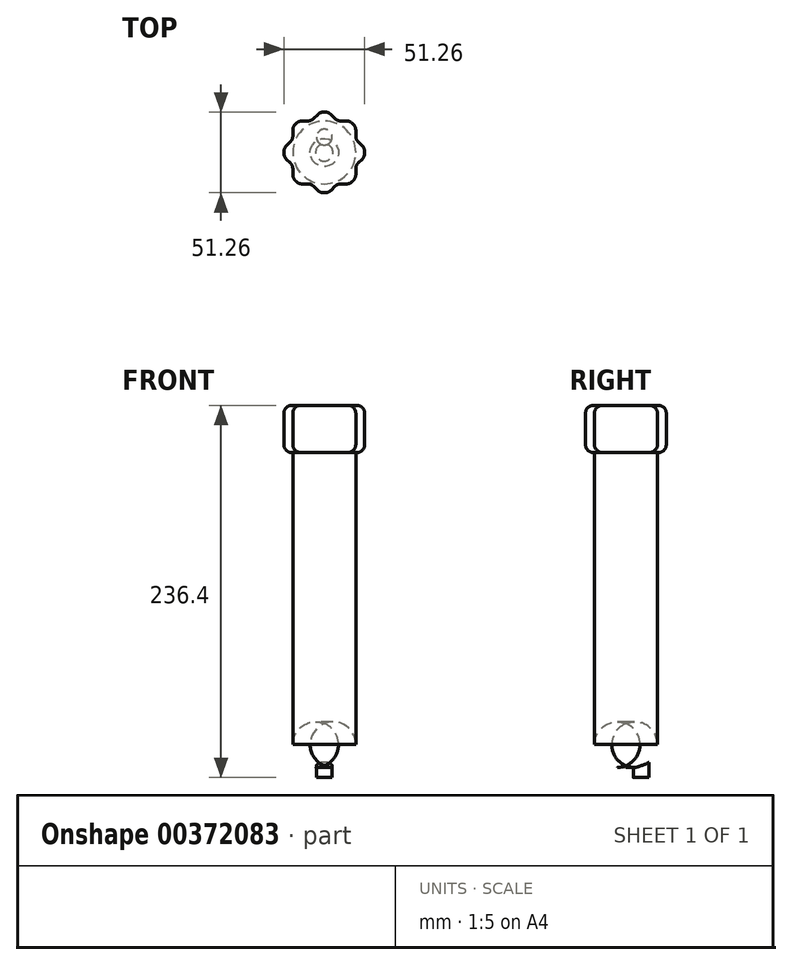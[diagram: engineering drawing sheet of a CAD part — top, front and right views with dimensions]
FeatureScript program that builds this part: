
annotation { "Feature Type Name" : "Feature", "Feature Type Description" : "" }
export const myFeature = defineFeature(function(context is Context, id is Id, definition is map)
    precondition{}
    {
        {
            var Q0;
            Q0=qCreatedBy(makeId("Top.planeOp"),FACE);
            var sketch = newSketch(context, id + "F0", { "sketchPlane" : qUnion([Q0])});
            skCircle(sketch, "E0", {"center": v(0, 0) * mm, "radius": 20 * mm});
            skSolve(sketch);
        }
        {
            var Q0;
            Q0 = qSketchRegion(id + "F0", true);
            extrude(context, id + "F1", {"entities" : qUnion([Q0]), "depth" : 200 * mm});
        }
        {
            var Q0;
            Q0=makeQuery(id+"F1.opExtrude","CAP_FACE",FACE,{"disambiguationData":[OSD([sQuery(id+"F0.wireOp",EDGE,"E0")])],"isStart":false});
            var sketch = newSketch(context, id + "F2", { "sketchPlane" : qUnion([Q0])});
            skLineSegment(sketch, "E1.bottom", {"start": v(-16.03, -20) * mm, "end": v(-8.28, -20) * mm});
            skLineSegment(sketch, "E1.top", {"start": v(-16.03, 20) * mm, "end": v(-8.28, 20) * mm});
            skLineSegment(sketch, "E1.left", {"start": v(-20, -16.03) * mm, "end": v(-20, -8.28) * mm});
            skLineSegment(sketch, "E1.right", {"start": v(20, -16.03) * mm, "end": v(20, -8.28) * mm});
            skPoint(sketch, "E1.middle", {"position": v(0, 0) * mm});
            skLineSegment(sketch, "E2.1.0", {"start": v(-25.48, -2.8) * mm, "end": v(-20, -8.28) * mm});
            skLineSegment(sketch, "E2.1.1", {"start": v(-2.8, 25.48) * mm, "end": v(-8.28, 20) * mm});
            skLineSegment(sketch, "E2.1.2", {"start": v(2.8, 25.48) * mm, "end": v(8.28, 20) * mm});
            skLineSegment(sketch, "E2.1.3", {"start": v(25.48, -2.8) * mm, "end": v(20, -8.28) * mm});
            skLineSegment(sketch, "E2.anchor1", {"start": v(0, 0) * mm, "end": v(20, -20) * mm, "construction": true});
            skLineSegment(sketch, "E2.anchor2", {"start": v(0, 0) * mm, "end": v(-28.28, 0) * mm, "construction": true});
            skArc(sketch, "E3", {"start": v(2.8, 25.48) * mm, "mid": v(0, 25.63) * mm, "end": v(-2.8, 25.48) * mm});
            skPoint(sketch, "E4.orphan", {"position": v(28.28, 0) * mm});
            skPoint(sketch, "E5.orphan", {"position": v(20, 20) * mm});
            skPoint(sketch, "E6.orphan", {"position": v(0, 28.28) * mm});
            skPoint(sketch, "E7.orphan", {"position": v(-20, 20) * mm});
            skPoint(sketch, "E8.orphan", {"position": v(-20, -20) * mm});
            skPoint(sketch, "E9.orphan", {"position": v(0, -28.28) * mm});
            skArc(sketch, "E10.trimOffspring", {"start": v(20, 16.03) * mm, "mid": v(18.12, 18.12) * mm, "end": v(16.03, 20) * mm});
            skArc(sketch, "E11.trimOffspring", {"start": v(25.48, -2.8) * mm, "mid": v(25.63, 0) * mm, "end": v(25.48, 2.8) * mm});
            skArc(sketch, "E12.trimOffspring", {"start": v(16.03, -20) * mm, "mid": v(18.12, -18.12) * mm, "end": v(20, -16.03) * mm});
            skArc(sketch, "E13.trimOffspring", {"start": v(-2.8, -25.48) * mm, "mid": v(0, -25.63) * mm, "end": v(2.8, -25.48) * mm});
            skArc(sketch, "E14.trimOffspring", {"start": v(-20, -16.03) * mm, "mid": v(-18.12, -18.12) * mm, "end": v(-16.03, -20) * mm});
            skArc(sketch, "E15.trimOffspring", {"start": v(-25.48, 2.8) * mm, "mid": v(-25.63, 0) * mm, "end": v(-25.48, -2.8) * mm});
            skArc(sketch, "E16.trimOffspring", {"start": v(-16.03, 20) * mm, "mid": v(-18.12, 18.12) * mm, "end": v(-20, 16.03) * mm});
            skLineSegment(sketch, "E17.trimOffspring", {"start": v(20, 8.28) * mm, "end": v(20, 16.03) * mm});
            skLineSegment(sketch, "E18.trimOffspring", {"start": v(20, 8.28) * mm, "end": v(25.48, 2.8) * mm});
            skLineSegment(sketch, "E19.trimOffspring", {"start": v(8.28, 20) * mm, "end": v(16.03, 20) * mm});
            skLineSegment(sketch, "E20.trimOffspring", {"start": v(-20, 8.28) * mm, "end": v(-25.48, 2.8) * mm});
            skLineSegment(sketch, "E21.trimOffspring", {"start": v(-20, 8.28) * mm, "end": v(-20, 16.03) * mm});
            skLineSegment(sketch, "E22.trimOffspring", {"start": v(-8.28, -20) * mm, "end": v(-2.8, -25.48) * mm});
            skLineSegment(sketch, "E23.trimOffspring", {"start": v(8.28, -20) * mm, "end": v(16.03, -20) * mm});
            skLineSegment(sketch, "E24.trimOffspring", {"start": v(8.28, -20) * mm, "end": v(2.8, -25.48) * mm});
            skSolve(sketch);
        }
        {
            var Q0;
            Q0=makeQuery(id+"F2.imprint","IMPRINT",FACE,{"disambiguationData":[TD([[makeQuery(id+"F2.imprint","IMPRINT",EDGE,{"derivedFrom":sQuery(id+"F2.wireOp",EDGE,"E1.bottom")}),1.0]])]});
            var Q1;
            Q1=makeQuery(id+"F2.imprint","IMPRINT",FACE,{"disambiguationData":[TD([[makeQuery(id+"F2.imprint","IMPRINT",EDGE,{"derivedFrom":makeQuery(id+"F1.opExtrude","CAP_EDGE",EDGE,{"disambiguationData":[OSD([sQuery(id+"F0.wireOp",EDGE,"E0")])],"isStart":false})}),1.0]])]});
            extrude(context, id + "F3", {"entities" : qUnion([Q0, Q1]), "depth" : 30 * mm});
        }
        {
            var Q0;
            Q0=makeQuery(id+"F3.opExtrude","SWEPT_EDGE",EDGE,{"disambiguationData":[OSD([sQuery(id+"F2.wireOp",EDGE,"E2.1.2"),sQuery(id+"F2.wireOp",EDGE,"E3")])]});
            var Q1;
            Q1=makeQuery(id+"F3.opExtrude","SWEPT_EDGE",EDGE,{"disambiguationData":[OSD([sQuery(id+"F2.wireOp",EDGE,"E2.1.1"),sQuery(id+"F2.wireOp",EDGE,"E3")])]});
            var Q2;
            Q2=makeQuery(id+"F3.opExtrude","SWEPT_EDGE",EDGE,{"disambiguationData":[OSD([sQuery(id+"F2.wireOp",EDGE,"E1.top"),sQuery(id+"F2.wireOp",EDGE,"E16.trimOffspring")])]});
            var Q3;
            Q3=makeQuery(id+"F3.opExtrude","SWEPT_EDGE",EDGE,{"disambiguationData":[OSD([sQuery(id+"F2.wireOp",EDGE,"E2.1.2"),sQuery(id+"F2.wireOp",EDGE,"E19.trimOffspring")])]});
            var Q4;
            Q4=makeQuery(id+"F3.opExtrude","SWEPT_EDGE",EDGE,{"disambiguationData":[OSD([sQuery(id+"F2.wireOp",EDGE,"E10.trimOffspring"),sQuery(id+"F2.wireOp",EDGE,"E19.trimOffspring")])]});
            var Q5;
            Q5=makeQuery(id+"F3.opExtrude","SWEPT_EDGE",EDGE,{"disambiguationData":[OSD([sQuery(id+"F2.wireOp",EDGE,"E10.trimOffspring"),sQuery(id+"F2.wireOp",EDGE,"E17.trimOffspring")])]});
            var Q6;
            Q6=makeQuery(id+"F3.opExtrude","SWEPT_EDGE",EDGE,{"disambiguationData":[OSD([sQuery(id+"F2.wireOp",EDGE,"E17.trimOffspring"),sQuery(id+"F2.wireOp",EDGE,"E18.trimOffspring")])]});
            var Q7;
            Q7=makeQuery(id+"F3.opExtrude","SWEPT_EDGE",EDGE,{"disambiguationData":[OSD([sQuery(id+"F2.wireOp",EDGE,"E1.top"),sQuery(id+"F2.wireOp",EDGE,"E2.1.1")])]});
            var Q8;
            Q8=makeQuery(id+"F3.opExtrude","SWEPT_EDGE",EDGE,{"disambiguationData":[OSD([sQuery(id+"F2.wireOp",EDGE,"E11.trimOffspring"),sQuery(id+"F2.wireOp",EDGE,"E18.trimOffspring")])]});
            var Q9;
            Q9=makeQuery(id+"F3.opExtrude","SWEPT_EDGE",EDGE,{"disambiguationData":[OSD([sQuery(id+"F2.wireOp",EDGE,"E2.1.3"),sQuery(id+"F2.wireOp",EDGE,"E11.trimOffspring")])]});
            var Q10;
            Q10=makeQuery(id+"F3.opExtrude","SWEPT_EDGE",EDGE,{"disambiguationData":[OSD([sQuery(id+"F2.wireOp",EDGE,"E1.right"),sQuery(id+"F2.wireOp",EDGE,"E2.1.3")])]});
            var Q11;
            Q11=makeQuery(id+"F3.opExtrude","SWEPT_EDGE",EDGE,{"disambiguationData":[OSD([sQuery(id+"F2.wireOp",EDGE,"E1.right"),sQuery(id+"F2.wireOp",EDGE,"E12.trimOffspring")])]});
            var Q12;
            Q12=makeQuery(id+"F3.opExtrude","SWEPT_EDGE",EDGE,{"disambiguationData":[OSD([sQuery(id+"F2.wireOp",EDGE,"E12.trimOffspring"),sQuery(id+"F2.wireOp",EDGE,"E23.trimOffspring")])]});
            var Q13;
            Q13=makeQuery(id+"F3.opExtrude","SWEPT_EDGE",EDGE,{"disambiguationData":[OSD([sQuery(id+"F2.wireOp",EDGE,"E23.trimOffspring"),sQuery(id+"F2.wireOp",EDGE,"E24.trimOffspring")])]});
            var Q14;
            Q14=makeQuery(id+"F3.opExtrude","SWEPT_EDGE",EDGE,{"disambiguationData":[OSD([sQuery(id+"F2.wireOp",EDGE,"E13.trimOffspring"),sQuery(id+"F2.wireOp",EDGE,"E24.trimOffspring")])]});
            var Q15;
            Q15=makeQuery(id+"F3.opExtrude","SWEPT_EDGE",EDGE,{"disambiguationData":[OSD([sQuery(id+"F2.wireOp",EDGE,"E13.trimOffspring"),sQuery(id+"F2.wireOp",EDGE,"E22.trimOffspring")])]});
            var Q16;
            Q16=makeQuery(id+"F3.opExtrude","SWEPT_EDGE",EDGE,{"disambiguationData":[OSD([sQuery(id+"F2.wireOp",EDGE,"E1.bottom"),sQuery(id+"F2.wireOp",EDGE,"E14.trimOffspring")])]});
            var Q17;
            Q17=makeQuery(id+"F3.opExtrude","SWEPT_EDGE",EDGE,{"disambiguationData":[OSD([sQuery(id+"F2.wireOp",EDGE,"E1.bottom"),sQuery(id+"F2.wireOp",EDGE,"E22.trimOffspring")])]});
            var Q18;
            Q18=makeQuery(id+"F3.opExtrude","SWEPT_EDGE",EDGE,{"disambiguationData":[OSD([sQuery(id+"F2.wireOp",EDGE,"E1.left"),sQuery(id+"F2.wireOp",EDGE,"E14.trimOffspring")])]});
            var Q19;
            Q19=makeQuery(id+"F3.opExtrude","SWEPT_EDGE",EDGE,{"disambiguationData":[OSD([sQuery(id+"F2.wireOp",EDGE,"E1.left"),sQuery(id+"F2.wireOp",EDGE,"E2.1.0")])]});
            var Q20;
            Q20=makeQuery(id+"F3.opExtrude","SWEPT_EDGE",EDGE,{"disambiguationData":[OSD([sQuery(id+"F2.wireOp",EDGE,"E2.1.0"),sQuery(id+"F2.wireOp",EDGE,"E15.trimOffspring")])]});
            var Q21;
            Q21=makeQuery(id+"F3.opExtrude","SWEPT_EDGE",EDGE,{"disambiguationData":[OSD([sQuery(id+"F2.wireOp",EDGE,"E15.trimOffspring"),sQuery(id+"F2.wireOp",EDGE,"E20.trimOffspring")])]});
            var Q22;
            Q22=makeQuery(id+"F3.opExtrude","SWEPT_EDGE",EDGE,{"disambiguationData":[OSD([sQuery(id+"F2.wireOp",EDGE,"E20.trimOffspring"),sQuery(id+"F2.wireOp",EDGE,"E21.trimOffspring")])]});
            var Q23;
            Q23=makeQuery(id+"F3.opExtrude","SWEPT_EDGE",EDGE,{"disambiguationData":[OSD([sQuery(id+"F2.wireOp",EDGE,"E16.trimOffspring"),sQuery(id+"F2.wireOp",EDGE,"E21.trimOffspring")])]});
            fillet(context, id + "F4", {"entities" : qUnion([Q0, Q1, Q2, Q3, Q4, Q5, Q6, Q7, Q8, Q9, Q10, Q11, Q12, Q13, Q14, Q15, Q16, Q17, Q18, Q19, Q20, Q21, Q22, Q23]), "radius" : 5 * mm, "tangentPropagation" : true, "allowEdgeOverflow" : false});
        }
        {
            var Q0;
            Q0=makeQuery(id+"F3.opExtrude","CAP_FACE",FACE,{"disambiguationData":[OSD([sQuery(id+"F2.wireOp",EDGE,"E1.bottom"),sQuery(id+"F2.wireOp",EDGE,"E1.top"),sQuery(id+"F2.wireOp",EDGE,"E1.left"),sQuery(id+"F2.wireOp",EDGE,"E1.right"),sQuery(id+"F2.wireOp",EDGE,"E2.1.0"),sQuery(id+"F2.wireOp",EDGE,"E2.1.1"),sQuery(id+"F2.wireOp",EDGE,"E2.1.2"),sQuery(id+"F2.wireOp",EDGE,"E2.1.3"),sQuery(id+"F2.wireOp",EDGE,"E3"),sQuery(id+"F2.wireOp",EDGE,"E10.trimOffspring"),sQuery(id+"F2.wireOp",EDGE,"E11.trimOffspring"),sQuery(id+"F2.wireOp",EDGE,"E12.trimOffspring"),sQuery(id+"F2.wireOp",EDGE,"E13.trimOffspring"),sQuery(id+"F2.wireOp",EDGE,"E14.trimOffspring"),sQuery(id+"F2.wireOp",EDGE,"E15.trimOffspring"),sQuery(id+"F2.wireOp",EDGE,"E16.trimOffspring"),sQuery(id+"F2.wireOp",EDGE,"E17.trimOffspring"),sQuery(id+"F2.wireOp",EDGE,"E18.trimOffspring"),sQuery(id+"F2.wireOp",EDGE,"E19.trimOffspring"),sQuery(id+"F2.wireOp",EDGE,"E20.trimOffspring"),sQuery(id+"F2.wireOp",EDGE,"E21.trimOffspring"),sQuery(id+"F2.wireOp",EDGE,"E22.trimOffspring"),sQuery(id+"F2.wireOp",EDGE,"E23.trimOffspring"),sQuery(id+"F2.wireOp",EDGE,"E24.trimOffspring")])],"isStart":true});
            var Q1;
            Q1=makeQuery(id+"F3.opExtrude","CAP_FACE",FACE,{"disambiguationData":[OSD([sQuery(id+"F2.wireOp",EDGE,"E1.bottom"),sQuery(id+"F2.wireOp",EDGE,"E1.top"),sQuery(id+"F2.wireOp",EDGE,"E1.left"),sQuery(id+"F2.wireOp",EDGE,"E1.right"),sQuery(id+"F2.wireOp",EDGE,"E2.1.0"),sQuery(id+"F2.wireOp",EDGE,"E2.1.1"),sQuery(id+"F2.wireOp",EDGE,"E2.1.2"),sQuery(id+"F2.wireOp",EDGE,"E2.1.3"),sQuery(id+"F2.wireOp",EDGE,"E3"),sQuery(id+"F2.wireOp",EDGE,"E10.trimOffspring"),sQuery(id+"F2.wireOp",EDGE,"E11.trimOffspring"),sQuery(id+"F2.wireOp",EDGE,"E12.trimOffspring"),sQuery(id+"F2.wireOp",EDGE,"E13.trimOffspring"),sQuery(id+"F2.wireOp",EDGE,"E14.trimOffspring"),sQuery(id+"F2.wireOp",EDGE,"E15.trimOffspring"),sQuery(id+"F2.wireOp",EDGE,"E16.trimOffspring"),sQuery(id+"F2.wireOp",EDGE,"E17.trimOffspring"),sQuery(id+"F2.wireOp",EDGE,"E18.trimOffspring"),sQuery(id+"F2.wireOp",EDGE,"E19.trimOffspring"),sQuery(id+"F2.wireOp",EDGE,"E20.trimOffspring"),sQuery(id+"F2.wireOp",EDGE,"E21.trimOffspring"),sQuery(id+"F2.wireOp",EDGE,"E22.trimOffspring"),sQuery(id+"F2.wireOp",EDGE,"E23.trimOffspring"),sQuery(id+"F2.wireOp",EDGE,"E24.trimOffspring")])],"isStart":false});
            fillet(context, id + "F5", {"entities" : qUnion([Q0, Q1]), "radius" : 5 * mm, "tangentPropagation" : true, "allowEdgeOverflow" : false});
        }
        {
            var Q0;
            Q0=makeQuery(id+"F1.opExtrude","CAP_FACE",FACE,{"disambiguationData":[OSD([sQuery(id+"F0.wireOp",EDGE,"E0")])],"isStart":true});
            fillet(context, id + "F6", {"entities" : qUnion([Q0]), "radius" : 14.5 * mm, "tangentPropagation" : true, "allowEdgeOverflow" : false});
        }
        {
            var Q0;
            Q0=makeQuery(id+"F1.opExtrude","CAP_FACE",FACE,{"disambiguationData":[OSD([sQuery(id+"F0.wireOp",EDGE,"E0")])],"isStart":true});
            var sketch = newSketch(context, id + "F7", { "sketchPlane" : qUnion([Q0])});
            skCircle(sketch, "E25", {"center": v(0, 10.47) * mm, "radius": 4.6 * mm});
            skCircle(sketch, "E26", {"center": v(0, -9.74) * mm, "radius": 5 * mm});
            skSolve(sketch);
        }
        {
            var Q0;
            Q0 = qSketchRegion(id + "F7", true);
            extrude(context, id + "F8", {"entities" : qUnion([Q0]), "operationType" : NewBodyOperationType.ADD, "endBound" : BoundingType.SYMMETRIC, "depth" : 12.8 * mm});
        }
    });
